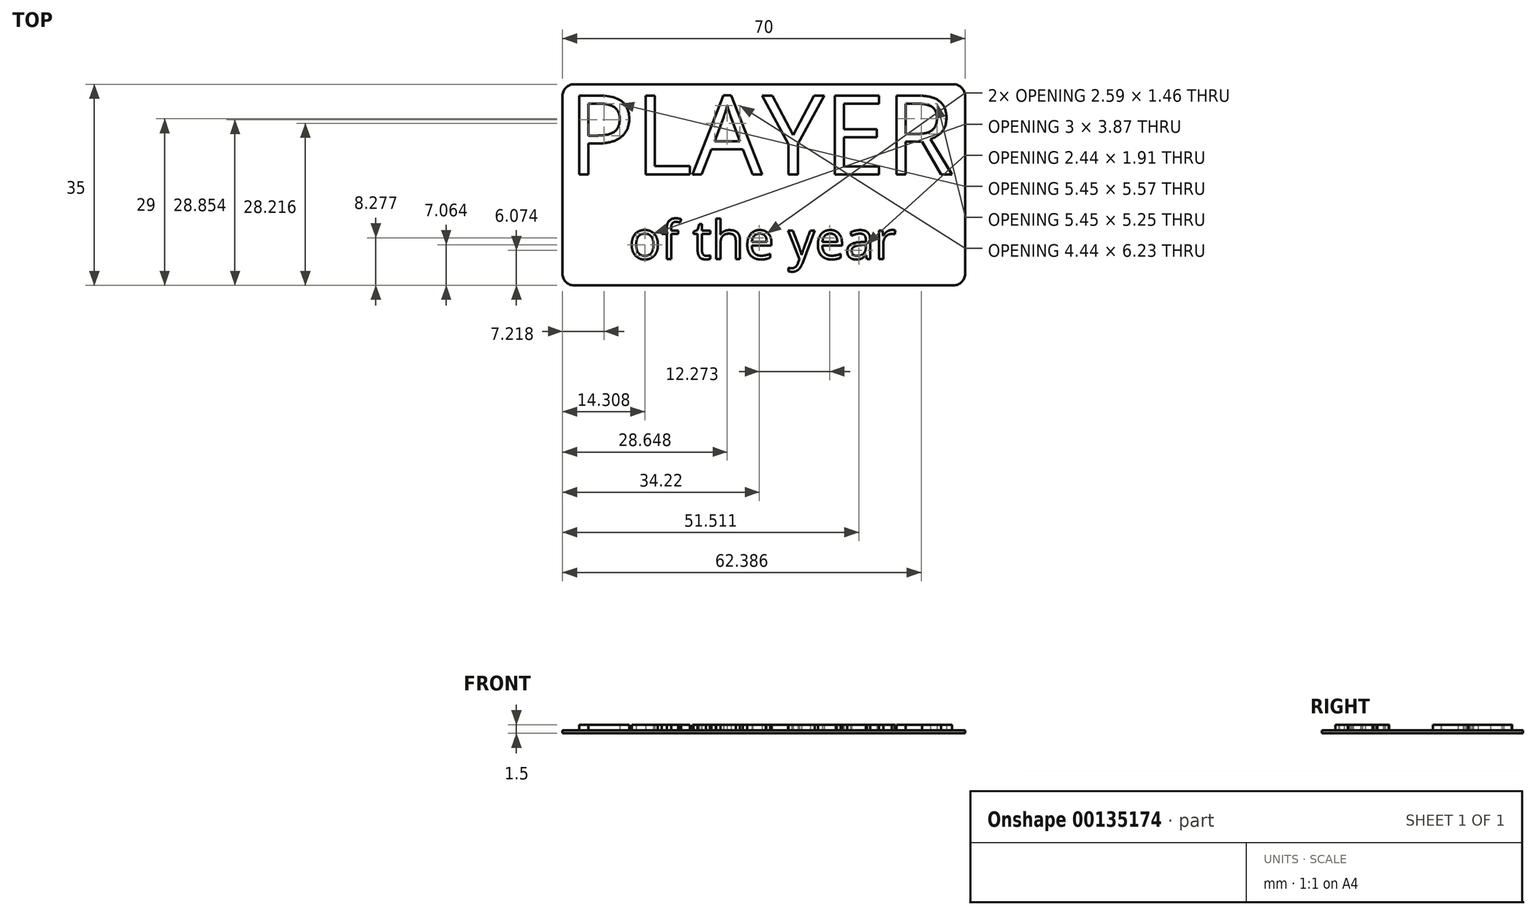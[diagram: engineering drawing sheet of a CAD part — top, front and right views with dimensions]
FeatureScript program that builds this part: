
annotation { "Feature Type Name" : "Feature", "Feature Type Description" : "" }
export const myFeature = defineFeature(function(context is Context, id is Id, definition is map)
    precondition{}
    {
        {
            var Q0;
            Q0=qCreatedBy(makeId("Top.planeOp"),FACE);
            var sketch = newSketch(context, id + "F0", { "sketchPlane" : qUnion([Q0])});
            skLineSegment(sketch, "E0.bottom", {"start": v(-20.28, -3.51) * mm, "end": v(49.72, -3.51) * mm});
            skLineSegment(sketch, "E0.top", {"start": v(-20.28, -38.51) * mm, "end": v(49.72, -38.51) * mm});
            skLineSegment(sketch, "E0.left", {"start": v(-20.28, -3.51) * mm, "end": v(-20.28, -38.51) * mm});
            skLineSegment(sketch, "E0.right", {"start": v(49.72, -3.51) * mm, "end": v(49.72, -38.51) * mm});
            skSolve(sketch);
        }
        {
            var Q0;
            Q0=makeQuery(id+"F0.imprint","IMPRINT",FACE,{"disambiguationData":[TD([[makeQuery(id+"F0.imprint","IMPRINT",EDGE,{"derivedFrom":sQuery(id+"F0.wireOp",EDGE,"E0.bottom")}),-1.0]])]});
            extrude(context, id + "F1", {"entities" : qUnion([Q0]), "oppositeDirection" : true, "depth" : 0.5 * mm});
        }
        {
            var Q0;
            Q0=makeQuery(id+"F1.opExtrude","SWEPT_EDGE",EDGE,{"disambiguationData":[OSD([sQuery(id+"F0.wireOp",EDGE,"E0.top"),sQuery(id+"F0.wireOp",EDGE,"E0.right")])]});
            var Q1;
            Q1=makeQuery(id+"F1.opExtrude","SWEPT_EDGE",EDGE,{"disambiguationData":[OSD([sQuery(id+"F0.wireOp",EDGE,"E0.top"),sQuery(id+"F0.wireOp",EDGE,"E0.left")])]});
            var Q2;
            Q2=makeQuery(id+"F1.opExtrude","SWEPT_EDGE",EDGE,{"disambiguationData":[OSD([sQuery(id+"F0.wireOp",EDGE,"E0.bottom"),sQuery(id+"F0.wireOp",EDGE,"E0.left")])]});
            var Q3;
            Q3=makeQuery(id+"F1.opExtrude","SWEPT_EDGE",EDGE,{"disambiguationData":[OSD([sQuery(id+"F0.wireOp",EDGE,"E0.bottom"),sQuery(id+"F0.wireOp",EDGE,"E0.right")])]});
            fillet(context, id + "F2", {"entities" : qUnion([Q0, Q1, Q2, Q3]), "radius" : 2 * mm, "tangentPropagation" : true, "allowEdgeOverflow" : false});
        }
        {
            var Q0;
            Q0=qCreatedBy(makeId("Top.planeOp"),FACE);
            var sketch = newSketch(context, id + "F3", { "sketchPlane" : qUnion([Q0])});
            skPoint(sketch, "E1", {"position": v(14.72, -38.51) * mm});
            skText(sketch, "E2", { "text": "of the year", "fontName": "OpenSans-Regular.ttf"});
            skText(sketch, "E3", { "text": "PLAYER", "fontName": "OpenSans-Regular.ttf"});
            skLineSegment(sketch, "E4.0", {"start": v(-18.28, -3.51) * mm, "end": v(47.72, -3.51) * mm});
            skPoint(sketch, "E5", {"position": v(14.72, -3.51) * mm});
            skLineSegment(sketch, "E6.0", {"start": v(-18.28, -38.51) * mm, "end": v(47.72, -38.51) * mm});
            const initialGuessF3  = {"E2": [-0.00877, -0.03392, 1, 0, 0.00667], "E3": [-0.01927, -0.01921, 1, 0, 0.01384]};
            skSetInitialGuess(sketch, initialGuessF3);
            skSolve(sketch);
        }
        {
            var Q0;
            Q0=qSketchRegion(id+"F3",true);
            extrude(context, id + "F4", {"entities" : qUnion([Q0]), "depth" : 1 * mm});
        }
    });
